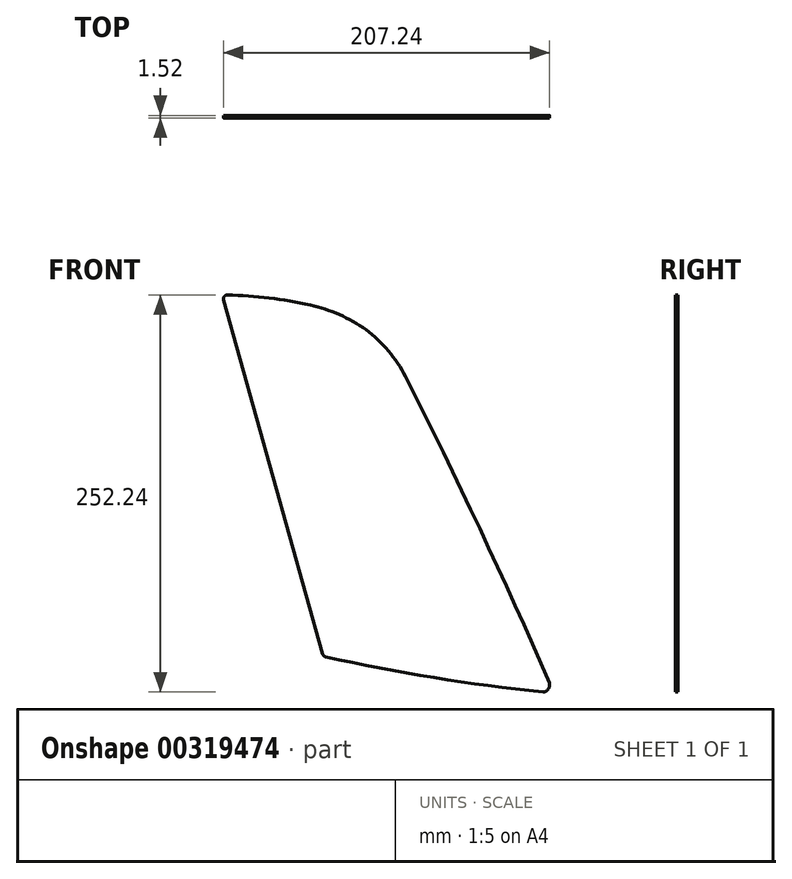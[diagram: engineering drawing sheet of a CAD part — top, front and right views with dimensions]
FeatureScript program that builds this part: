
annotation { "Feature Type Name" : "Feature", "Feature Type Description" : "" }
export const myFeature = defineFeature(function(context is Context, id is Id, definition is map)
    precondition{}
    {
        {
            var Q0;
            Q0=qCreatedBy(makeId("Front.planeOp"),FACE);
            var sketch = newSketch(context, id + "F0", { "sketchPlane" : qUnion([Q0])});
            skLineSegment(sketch, "E0", {"start": v(9.4, -86.13) * mm, "end": v(-48.25, 82.07) * mm});
            skLineSegment(sketch, "E1", {"start": v(-37.5, -110.02) * mm, "end": v(-100.5, 114.8) * mm});
            skArc(sketch, "E2", {"start": v(-35.6, -111.82) * mm, "mid": v(33.03, -125.01) * mm, "end": v(102.32, -134.2) * mm});
            skArc(sketch, "E3", {"start": v(102.32, -134.2) * mm, "mid": v(105.85, -132.26) * mm, "end": v(106.44, -128.27) * mm});
            skArc(sketch, "E4", {"start": v(106.44, -128.27) * mm, "mid": v(62.24, -30.36) * mm, "end": v(15.14, 66.19) * mm});
            skArc(sketch, "E5", {"start": v(15.14, 66.19) * mm, "mid": v(4.2, 82.49) * mm, "end": v(-10.03, 96.03) * mm});
            skArc(sketch, "E6", {"start": v(-10.03, 96.03) * mm, "mid": v(-26.96, 105.5) * mm, "end": v(-45.36, 111.67) * mm});
            skArc(sketch, "E7", {"start": v(-45.36, 111.67) * mm, "mid": v(-71.52, 116.03) * mm, "end": v(-97.97, 118.03) * mm});
            skPoint(sketch, "E8.visualSharp", {"position": v(-37.09, -111.49) * mm});
            skArc(sketch, "E8.filletArc", {"start": v(-37.5, -110.02) * mm, "mid": v(-36.8, -111.18) * mm, "end": v(-35.6, -111.82) * mm});
            skPoint(sketch, "E9.visualSharp", {"position": v(-101.42, 118.12) * mm});
            skArc(sketch, "E9.filletArc", {"start": v(-97.97, 118.03) * mm, "mid": v(-100.04, 117.06) * mm, "end": v(-100.5, 114.8) * mm});
            skSolve(sketch);
        }
        {
            var Q0;
            Q0=makeQuery(id+"F0.imprint","IMPRINT",FACE,{"disambiguationData":[TD([[makeQuery(id+"F0.imprint","IMPRINT",EDGE,{"derivedFrom":sQuery(id+"F0.wireOp",EDGE,"E1")}),-1.0]])]});
            extrude(context, id + "F1", {"entities" : qUnion([Q0]), "depth" : 1.52 * mm});
        }
    });
